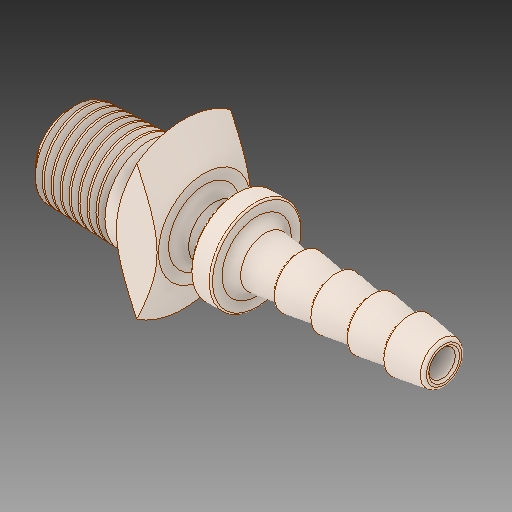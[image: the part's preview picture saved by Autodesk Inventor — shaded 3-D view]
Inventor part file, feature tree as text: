
AUTODESK INVENTOR PART (.ipt)
format: ipt  version: 2018 (Build 220112000, 112)  size: 736,256 bytes
history: native  units: in
note: dims shown in document units (in); Inventor stores cm internally (conversion verified against a paired STEP export)
features: fillet x1
ambient origin geometry x8: Origin, YZ Plane, XZ Plane, XY Plane, X Axis, Y Axis, Z Axis, Center Point
bodies: Solid1 (feature_tree)
feature tree (1):
  fillet  "Fillet3"  [1 undecoded]
note: 1 required parameter value undecoded (feature->parameter linkage not recoverable at this tier; creation-order binding heuristic only, values carry confidence <= 0.55)
